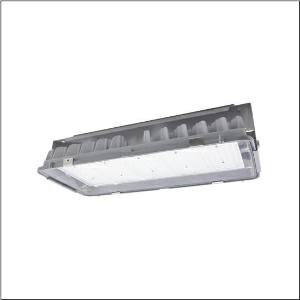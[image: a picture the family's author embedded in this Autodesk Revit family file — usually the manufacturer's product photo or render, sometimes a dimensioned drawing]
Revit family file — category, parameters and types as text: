
# Revit family: highbay_11xtreme_51hf61da4mma
name_source: partatom
category: Lighting Fixtures
units: mm (PartAtom-declared; Revit-internal decimal feet)

## family parameters
Cut with Voids When Loaded = No
Host = Face
Light Source = No
Part Type = Normal
Room Calculation Point = No
Round Connector Dimension = Use Diameter
Shared = No

## types (1)
- --- (1 x LED, 31500 lm, 170.8 W, 4000K)
    Apparent Load = 171 VA
    CIE Flux Codes = 88 96 99 100 100
    Color Rendering = 80
    Color Temperature = 4000K
    Default Elevation = 1800 mm
    Description = Highbay 11Xtreme, LED high bay luminaire, primary light control with lens, of PMMA, primary optical cover: cover, of toughened safety glass, light emission: direct distribution, primary light characteristic: symmetric, installation type: suspended mounting, surface-mounted, 1x LED module,for 1x LED, rated luminous flux: 31.500lm, luminous efficacy: 184lm/W, light colour: 840, colour temperature: 4000K, with cable H07RN-F 5x 1.5mm², mains connection: 220..240V, AC, 50/60Hz, cable length: 1,5m, rated input power: 171W, luminaire housing, of diecast aluminium, coated, silver, length: 595mm, width: 280mm, height: 195mm, protection rating (complete): IP66, insulation class (complete): insulation class I (protective earthing), certification: CE, ENEC, UKCA, protection symbol: D, ball protection: ball impact resistant according to DIN VDE 0710 part 13 (with chain suspension), impact resistance: IK08, permissible operating ambient temperature: -25..+60°C, reducing of maximum allowable ambient temperature of 5°C with ceiling mounting, packaging unit: 1 piece
    Height = 157 mm
    Lamp = 1 x LED
    Lamp Light Flux = 31500 lm
    Lamp Power = 170.8 W
    Lamp count = 1
    Length = 593 mm
    Luminous efficacy = 184 lm/W
    Manufacturer = Siteco
    ModVariant = No
    Model = 51HF61DA4MMA
    Mounting Place = Ceiling
    Mounting Type = Pendant
    Number of Poles = 1
    OnlyDefault = Yes
    Power Factor = 1
    Product Name = Highbay 11Xtreme
    Product group = LED high bay luminaire
    ProductGroupID = 903
    Protection Class = Protection class I
    Protection Degree = IP 66
    RLX_Detail_Level = 1
    RLX_Emergency_Light_Flux = 0 lm
    RLX_Emergency_Type = 0
    RLX_Emergency_Type_DB = No
    RlxData = <blob elided: 27881 chars, md5=10e95c5c>
    Socket = socket
    Standby Power = 0 W
    System Light Flux = 31501 lm
    System Power = 171 W
    Type Comments = factory setting: luminous flux: 100 % | dim-lin: 254 | 1132 mA
    Type Image = l_1258342.jpg
    URL = http://relux.com
    VarID = @adj_052809
    Voltage = 0 V
    Weight = 0.00 kg
    Width = 278 mm

## geometry (parser evidence)
native form markers: Blend x4, Sweep x11
no freeform markers — native parametric forms only
